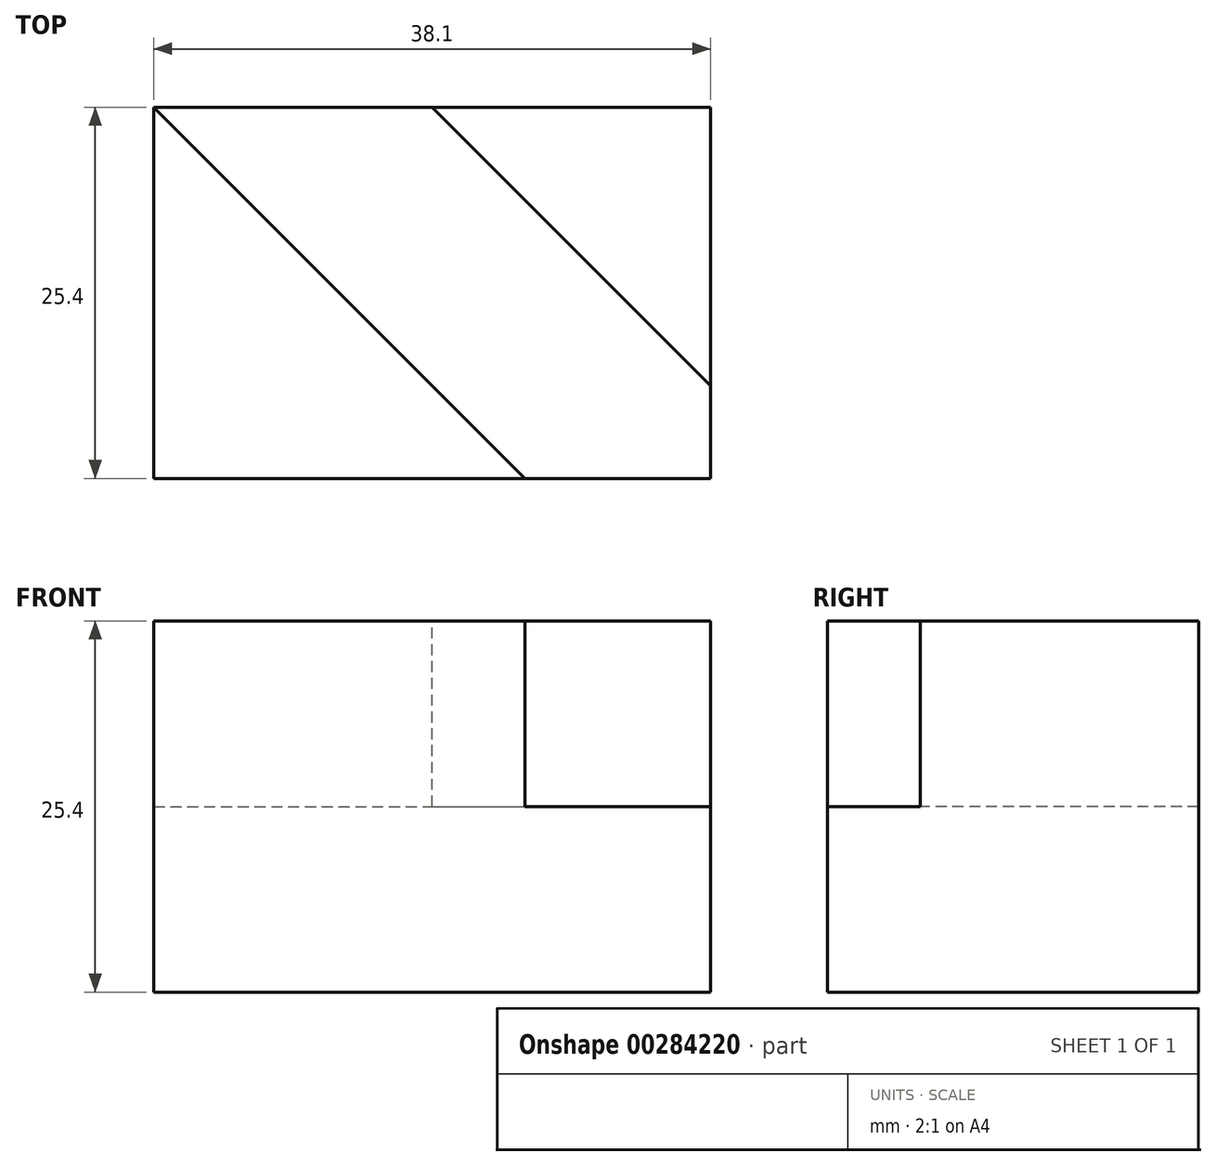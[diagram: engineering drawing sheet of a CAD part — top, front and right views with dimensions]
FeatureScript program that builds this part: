
annotation { "Feature Type Name" : "Feature", "Feature Type Description" : "" }
export const myFeature = defineFeature(function(context is Context, id is Id, definition is map)
    precondition{}
    {
        {
            var Q0;
            Q0=qCreatedBy(makeId("Front.planeOp"),FACE);
            var sketch = newSketch(context, id + "F0", { "sketchPlane" : qUnion([Q0])});
            skLineSegment(sketch, "E0", {"start": v(0, 0) * mm, "end": v(0, 25.4) * mm});
            skLineSegment(sketch, "E1", {"start": v(0, 25.4) * mm, "end": v(38.1, 25.4) * mm});
            skLineSegment(sketch, "E2", {"start": v(38.1, 25.4) * mm, "end": v(38.1, 0) * mm});
            skLineSegment(sketch, "E3", {"start": v(38.1, 0) * mm, "end": v(0, 0) * mm});
            skSolve(sketch);
        }
        {
            var Q0;
            Q0=makeQuery(id+"F0.imprint","IMPRINT",FACE,{"disambiguationData":[TD([[makeQuery(id+"F0.imprint","IMPRINT",EDGE,{"derivedFrom":sQuery(id+"F0.wireOp",EDGE,"E0")}),-1.0]])]});
            extrude(context, id + "F1", {"entities" : qUnion([Q0]), "depth" : 25.4 * mm});
        }
        {
            var Q0;
            Q0=makeQuery(id+"F1.opExtrude","SWEPT_FACE",FACE,{"disambiguationData":[OSD([sQuery(id+"F0.wireOp",EDGE,"E2")])]});
            var sketch = newSketch(context, id + "F2", { "sketchPlane" : qUnion([Q0])});
            skLineSegment(sketch, "E4", {"start": v(-19.05, 25.4) * mm, "end": v(-19.05, 12.7) * mm});
            skLineSegment(sketch, "E5", {"start": v(-19.05, 12.7) * mm, "end": v(-25.4, 12.7) * mm});
            skLineSegment(sketch, "E6", {"start": v(-25.4, 12.7) * mm, "end": v(-25.4, 25.4) * mm});
            skLineSegment(sketch, "E7", {"start": v(-25.4, 25.4) * mm, "end": v(-19.05, 25.4) * mm});
            skSolve(sketch);
        }
        {
            var Q0;
            Q0=makeQuery(id+"F2.imprint","IMPRINT",FACE,{"disambiguationData":[TD([[makeQuery(id+"F2.imprint","IMPRINT",EDGE,{"derivedFrom":sQuery(id+"F2.wireOp",EDGE,"E4")}),-1.0]])]});
            extrude(context, id + "F3", {"entities" : qUnion([Q0]), "operationType" : NewBodyOperationType.REMOVE, "oppositeDirection" : true, "depth" : 12.7 * mm});
        }
        {
            var Q0;
            Q0=makeQuery(id+"F1.opExtrude","SWEPT_FACE",FACE,{"disambiguationData":[OSD([sQuery(id+"F0.wireOp",EDGE,"E1")])]});
            var sketch = newSketch(context, id + "F4", { "sketchPlane" : qUnion([Q0])});
            skLineSegment(sketch, "E8", {"start": v(0, 0) * mm, "end": v(25.4, -25.4) * mm});
            skLineSegment(sketch, "E9", {"start": v(0, 0) * mm, "end": v(19.05, 0) * mm});
            skLineSegment(sketch, "E10", {"start": v(19.05, 0) * mm, "end": v(38.1, -19.05) * mm});
            skSolve(sketch);
        }
        {
            var Q0;
            Q0=makeQuery(id+"F4.imprint","IMPRINT",FACE,{"disambiguationData":[TD([[makeQuery(id+"F4.imprint","IMPRINT",EDGE,{"derivedFrom":sQuery(id+"F4.wireOp",EDGE,"E8")}),1.0]])]});
            extrude(context, id + "F5", {"entities" : qUnion([Q0]), "operationType" : NewBodyOperationType.REMOVE, "oppositeDirection" : true, "depth" : 12.7 * mm});
        }
    });
